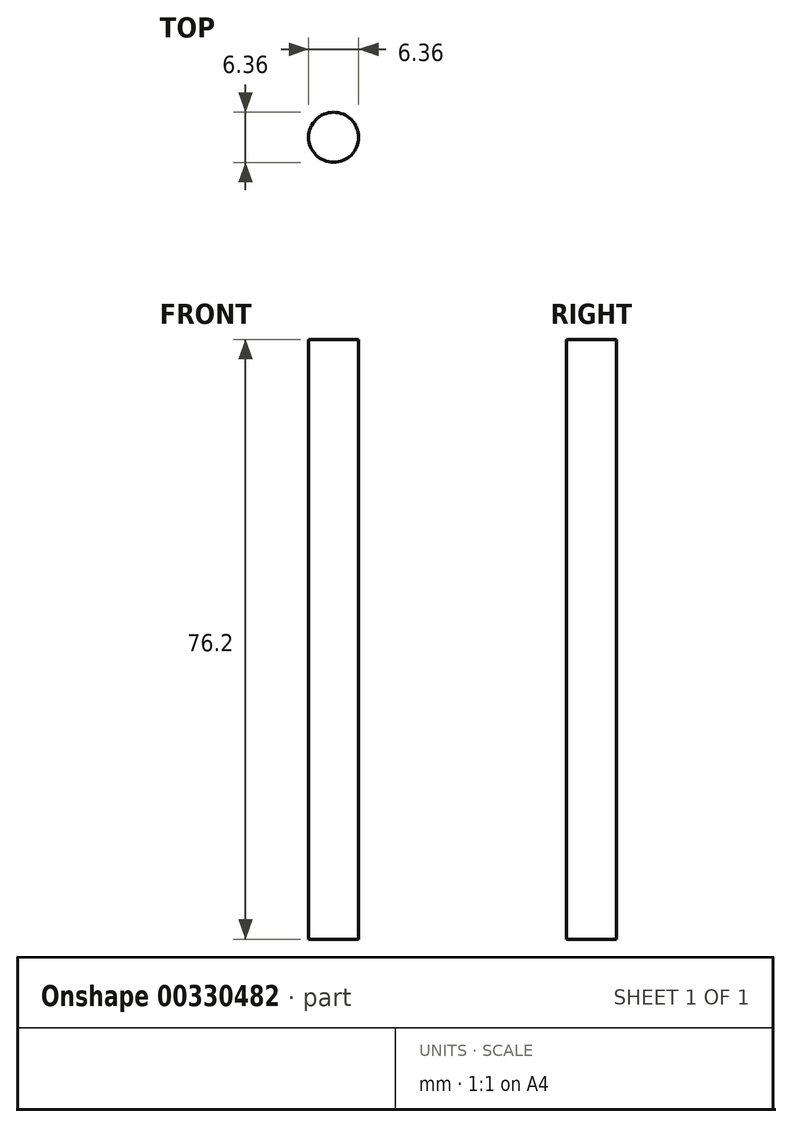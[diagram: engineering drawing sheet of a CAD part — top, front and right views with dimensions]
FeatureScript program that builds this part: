
annotation { "Feature Type Name" : "Feature", "Feature Type Description" : "" }
export const myFeature = defineFeature(function(context is Context, id is Id, definition is map)
    precondition{}
    {
        {
            var Q0;
            Q0=qCreatedBy(makeId("Top.planeOp"),FACE);
            var sketch = newSketch(context, id + "F0", { "sketchPlane" : qUnion([Q0])});
            skCircle(sketch, "E0", {"center": v(0, 0) * mm, "radius": 3.18 * mm});
            skSolve(sketch);
        }
        {
            var Q0;
            Q0=qSketchRegion(id+"F0",true);
            extrude(context, id + "F1", {"entities" : qUnion([Q0]), "depth" : 76.2 * mm});
        }
    });
